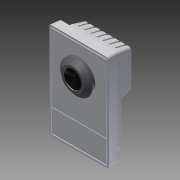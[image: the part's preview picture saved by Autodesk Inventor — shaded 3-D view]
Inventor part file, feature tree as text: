
AUTODESK INVENTOR PART (.ipt)
format: ipt  version: 2013 (Build 170138000, 138)  size: 766,464 bytes
history: native  units: in
note: dims shown in document units (in); Inventor stores cm internally (conversion verified against a paired STEP export)
features: fillet x1, other x1, imported_body x1
ambient origin geometry x8: Origin, YZ Plane, XZ Plane, XY Plane, X Axis, Y Axis, Z Axis, Center Point
feature tree (3):
  fillet  "Fillet18"  [1 undecoded]
  other  "AXIS M10111"
  imported_body  "Base1"
note: 1 required parameter value undecoded (feature->parameter linkage not recoverable at this tier; creation-order binding heuristic only, values carry confidence <= 0.55)
